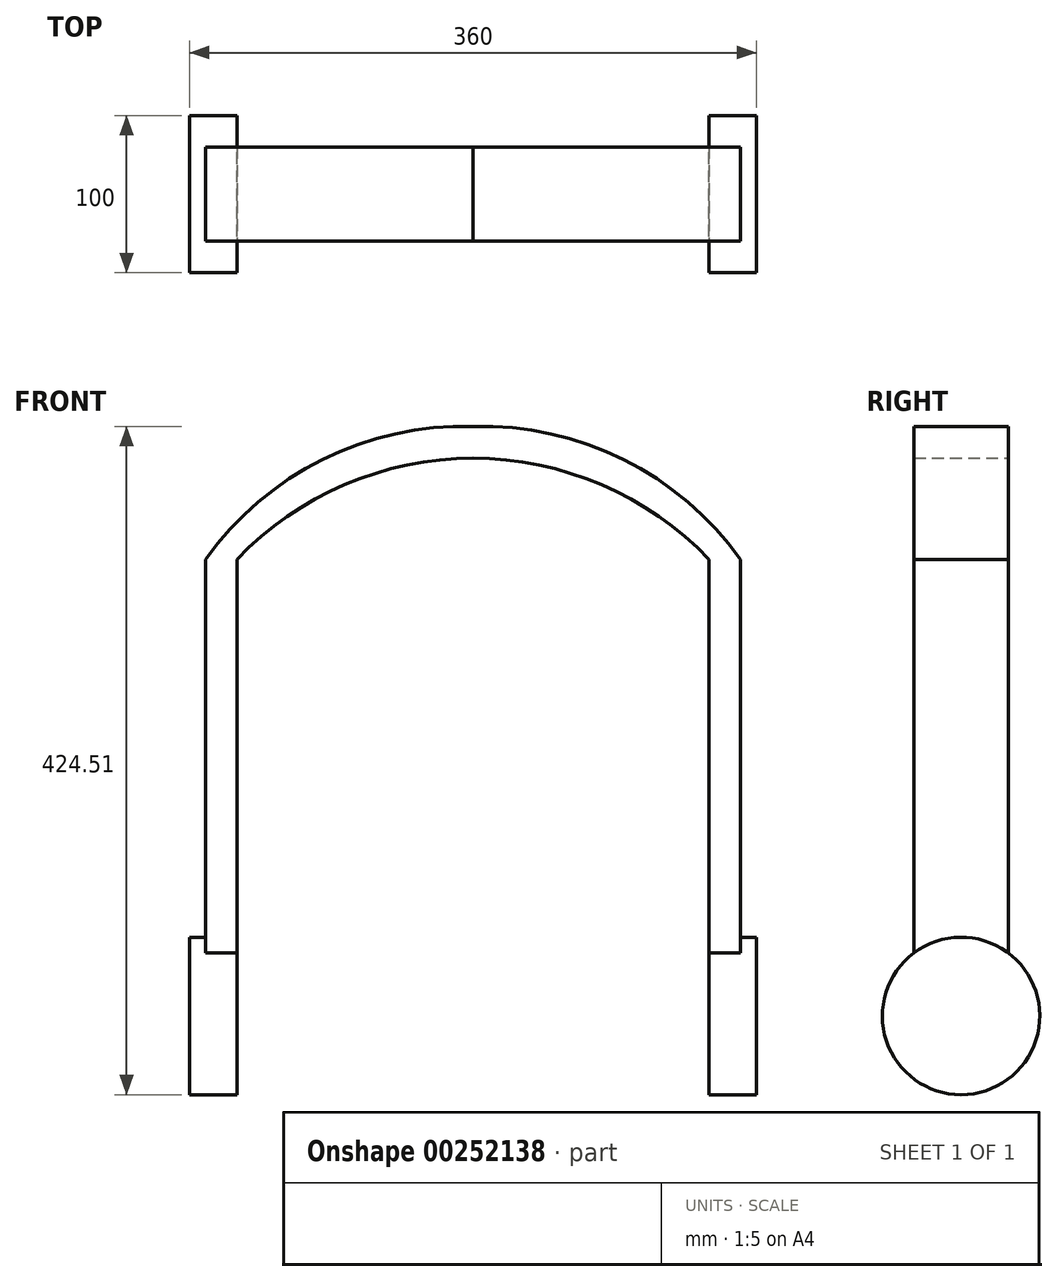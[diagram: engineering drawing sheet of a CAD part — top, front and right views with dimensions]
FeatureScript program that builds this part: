
annotation { "Feature Type Name" : "Feature", "Feature Type Description" : "" }
export const myFeature = defineFeature(function(context is Context, id is Id, definition is map)
    precondition{}
    {
        {
            var Q0;
            Q0=qCreatedBy(makeId("Right.planeOp"),FACE);
            var sketch = newSketch(context, id + "F0", { "sketchPlane" : qUnion([Q0])});
            skLineSegment(sketch, "E0.bottom", {"start": v(30, 145) * mm, "end": v(-30, 145) * mm});
            skLineSegment(sketch, "E0.left", {"start": v(30, 145) * mm, "end": v(30, -105) * mm});
            skLineSegment(sketch, "E0.right", {"start": v(-30, 145) * mm, "end": v(-30, -105) * mm});
            skPoint(sketch, "E0.middle", {"position": v(0, 0) * mm});
            skPoint(sketch, "E1.endSnap0", {"position": v(0, -145) * mm});
            skCircle(sketch, "E2", {"center": v(0, -145) * mm, "radius": 50 * mm});
            skPoint(sketch, "E3.orphan", {"position": v(-30, -145) * mm});
            skPoint(sketch, "E0.top.start.orphan", {"position": v(30, -145) * mm});
            skPoint(sketch, "E1.end.orphan", {"position": v(0, -113.74) * mm});
            skSolve(sketch);
        }
        {
            var Q0;
            {var subQ0=sQuery(id+"F0.wireOp",EDGE,"E2");var subQ1=makeQuery(id+"F0.imprint","INTERSECT",VERTEX,{"derivedFrom":[sQuery(id+"F0.wireOp",EDGE,"E0.left"),subQ0]});Q0=makeQuery(id+"F0.imprint","IMPRINT",FACE,{"disambiguationData":[TD([[makeQuery(id+"F0.imprint","IMPRINT",EDGE,{"disambiguationData":[TD([[subQ1,-1.0]])],"derivedFrom":subQ0}),1.0]])]});}
            extrude(context, id + "F1", {"entities" : qUnion([Q0]), "depth" : 30 * mm});
        }
        {
            var Q0;
            Q0 = qSketchRegion(id + "F0", true);
            extrude(context, id + "F2", {"entities" : qUnion([Q0]), "operationType" : NewBodyOperationType.ADD, "depth" : 20 * mm});
        }
        {
            var Q0;
            Q0=qCreatedBy(makeId("Front.planeOp"),FACE);
            var sketch = newSketch(context, id + "F3", { "sketchPlane" : qUnion([Q0])});
            skLineSegment(sketch, "E4.bottom", {"start": v(-59.25, 87.62) * mm, "end": v(-121.06, 87.62) * mm});
            skLineSegment(sketch, "E4.top", {"start": v(-59.25, 147.35) * mm, "end": v(-121.06, 147.35) * mm});
            skLineSegment(sketch, "E4.left", {"start": v(-59.25, 87.62) * mm, "end": v(-59.25, 147.35) * mm});
            skLineSegment(sketch, "E4.right", {"start": v(-121.06, 87.62) * mm, "end": v(-121.06, 147.35) * mm});
            skPoint(sketch, "E4.middle", {"position": v(-90.16, 117.48) * mm});
            skSolve(sketch);
        }
        {
            var Q0;
            Q0=makeQuery(id+"F3.imprint","IMPRINT",FACE,{"disambiguationData":[TD([[makeQuery(id+"F3.imprint","IMPRINT",EDGE,{"derivedFrom":sQuery(id+"F3.wireOp",EDGE,"E4.bottom")}),-1.0]])]});
            extrude(context, id + "F4", {"entities" : qUnion([Q0]), "operationType" : NewBodyOperationType.REMOVE, "endBound" : BoundingType.SYMMETRIC, "depth" : 100 * mm});
        }
        {
            var Q0;
            Q0=makeQuery(id+"F2.opExtrude","SWEPT_FACE",FACE,{"disambiguationData":[OSD([sQuery(id+"F0.wireOp",EDGE,"E0.left")])]});
            var sketch = newSketch(context, id + "F5", { "sketchPlane" : qUnion([Q0])});
            skPoint(sketch, "E5.orphan", {"position": v(130, 57) * mm});
            skPoint(sketch, "E6.orphan", {"position": v(130, 266.71) * mm});
            skLineSegment(sketch, "E7", {"start": v(150, 209.43) * mm, "end": v(150, 229.43) * mm});
            skPoint(sketch, "E8.end.orphan", {"position": v(130, 216.73) * mm});
            skPoint(sketch, "E9.center.orphan", {"position": v(120.12, 57) * mm});
            skPoint(sketch, "E9.start.orphan", {"position": v(130, 236.73) * mm});
            skArc(sketch, "E10", {"start": v(150, 209.43) * mm, "mid": v(68.47, 192.41) * mm, "end": v(0, 145) * mm});
            skArc(sketch, "E11", {"start": v(150, 229.43) * mm, "mid": v(54.48, 208.4) * mm, "end": v(-20, 145) * mm});
            skSolve(sketch);
        }
        {
            var Q0;
            Q0 = qSketchRegion(id + "F5", true);
            var Q1;
            Q1=makeQuery(id+"F5.imprint","IMPRINT",FACE,{"disambiguationData":[TD([[makeQuery(id+"F5.imprint","IMPRINT",EDGE,{"derivedFrom":sQuery(id+"F5.wireOp",EDGE,"E7")}),1.0]])]});
            extrude(context, id + "F6", {"entities" : qUnion([Q0, Q1]), "operationType" : NewBodyOperationType.ADD, "oppositeDirection" : true, "depth" : 60 * mm});
        }
        {
            var Q0;
            Q0=makeQuery(id+"F1.opExtrude","SWEPT_BODY",BODY,{"disambiguationData":[OSD([sQuery(id+"F0.wireOp",EDGE,"E2")])]});
            var Q1;
            Q1=makeQuery(id+"F6.opExtrude","SWEPT_FACE",FACE,{"disambiguationData":[OSD([sQuery(id+"F5.wireOp",EDGE,"E7")])]});
            mirror(context, id + "F7", {"operationType" : NewBodyOperationType.ADD, "entities" : qUnion([Q0]), "mirrorPlane" : qUnion([Q1])});
        }
    });
